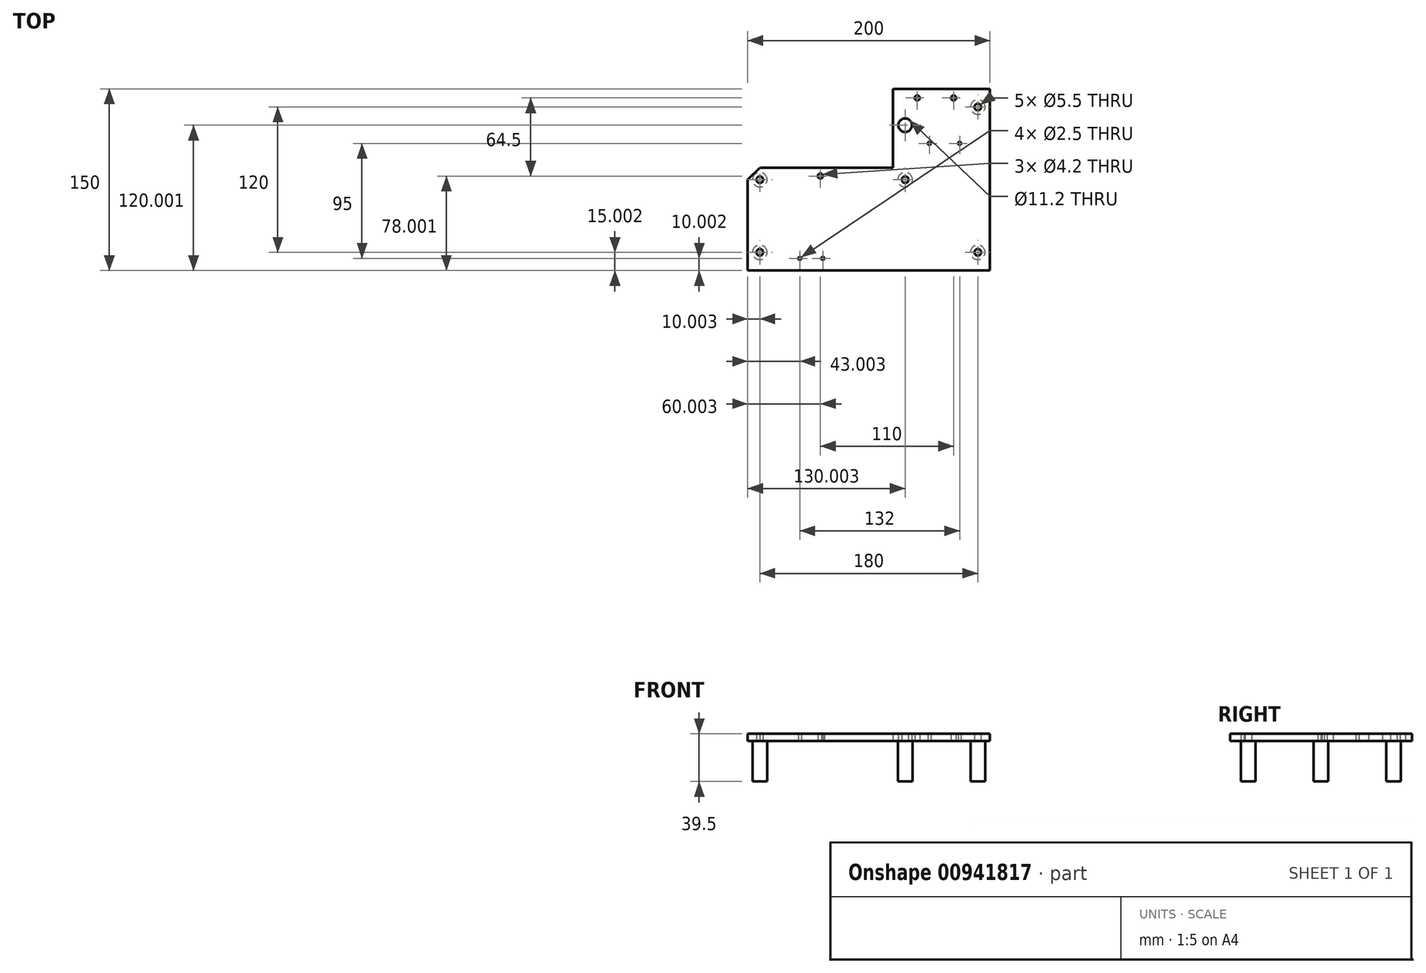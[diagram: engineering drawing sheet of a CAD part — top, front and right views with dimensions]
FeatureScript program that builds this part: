
annotation { "Feature Type Name" : "Feature", "Feature Type Description" : "" }
export const myFeature = defineFeature(function(context is Context, id is Id, definition is map)
    precondition{}
    {
        {
            var Q0;
            Q0=qCreatedBy(makeId("Top.planeOp"),FACE);
            var sketch = newSketch(context, id + "F0", { "sketchPlane" : qUnion([Q0])});
            skLineSegment(sketch, "E0", {"start": v(-126.29, 45.71) * mm, "end": v(-126.29, 110.71) * mm});
            skLineSegment(sketch, "E1", {"start": v(-46.29, 110.71) * mm, "end": v(-126.29, 110.71) * mm});
            skLineSegment(sketch, "E2", {"start": v(-46.29, -39.29) * mm, "end": v(-46.29, 110.71) * mm});
            skLineSegment(sketch, "E3", {"start": v(-246.29, -39.29) * mm, "end": v(-46.29, -39.29) * mm});
            skLineSegment(sketch, "E4", {"start": v(-246.29, 35.71) * mm, "end": v(-246.29, -39.29) * mm});
            skLineSegment(sketch, "E5", {"start": v(-236.29, 45.71) * mm, "end": v(-246.29, 35.71) * mm});
            skLineSegment(sketch, "E6", {"start": v(-236.29, 45.71) * mm, "end": v(-126.29, 45.71) * mm});
            skCircle(sketch, "E7", {"center": v(-116.29, 80.71) * mm, "radius": 5.6 * mm});
            skCircle(sketch, "E8", {"center": v(-106.29, 103.21) * mm, "radius": 2.1 * mm});
            skCircle(sketch, "E9", {"center": v(-76.29, 103.21) * mm, "radius": 2.1 * mm});
            skCircle(sketch, "E10", {"center": v(-71.29, 65.71) * mm, "radius": 1.25 * mm});
            skCircle(sketch, "E11", {"center": v(-96.29, 65.71) * mm, "radius": 1.25 * mm});
            skCircle(sketch, "E12", {"center": v(-184.29, -29.29) * mm, "radius": 1.25 * mm});
            skCircle(sketch, "E13", {"center": v(-203.29, -29.29) * mm, "radius": 1.25 * mm});
            skCircle(sketch, "E14", {"center": v(-186.29, 38.71) * mm, "radius": 2.1 * mm});
            skCircle(sketch, "E15", {"center": v(-236.29, 35.71) * mm, "radius": 2.75 * mm});
            skCircle(sketch, "E16", {"center": v(-56.29, -24.29) * mm, "radius": 2.75 * mm});
            skCircle(sketch, "E17", {"center": v(-116.29, 35.71) * mm, "radius": 2.75 * mm});
            skCircle(sketch, "E18", {"center": v(-56.29, 95.71) * mm, "radius": 2.75 * mm});
            skCircle(sketch, "E19", {"center": v(-116.29, 80.71) * mm, "radius": 2.75 * mm});
            skCircle(sketch, "E20", {"center": v(-236.29, -24.29) * mm, "radius": 2.75 * mm});
            skLineSegment(sketch, "E21", {"start": v(-116.29, 35.71) * mm, "end": v(-116.29, 38.21) * mm});
            skLineSegment(sketch, "E22", {"start": v(-116.29, 35.71) * mm, "end": v(-118.79, 35.71) * mm});
            skLineSegment(sketch, "E23", {"start": v(-116.29, 35.71) * mm, "end": v(-116.29, 33.21) * mm});
            skLineSegment(sketch, "E24", {"start": v(-116.29, 35.71) * mm, "end": v(-113.79, 35.71) * mm});
            skLineSegment(sketch, "E25", {"start": v(-116.29, 40.71) * mm, "end": v(-116.29, 40.96) * mm});
            skLineSegment(sketch, "E26", {"start": v(-121.29, 35.71) * mm, "end": v(-121.54, 35.71) * mm});
            skLineSegment(sketch, "E27", {"start": v(-116.29, 30.71) * mm, "end": v(-116.29, 30.46) * mm});
            skLineSegment(sketch, "E28", {"start": v(-111.29, 35.71) * mm, "end": v(-111.04, 35.71) * mm});
            skLineSegment(sketch, "E29", {"start": v(-116.29, 80.71) * mm, "end": v(-116.29, 83.21) * mm});
            skLineSegment(sketch, "E30", {"start": v(-116.29, 80.71) * mm, "end": v(-118.79, 80.71) * mm});
            skLineSegment(sketch, "E31", {"start": v(-116.29, 80.71) * mm, "end": v(-116.29, 78.21) * mm});
            skLineSegment(sketch, "E32", {"start": v(-116.29, 80.71) * mm, "end": v(-113.79, 80.71) * mm});
            skLineSegment(sketch, "E33", {"start": v(-116.29, 85.71) * mm, "end": v(-116.29, 85.96) * mm});
            skLineSegment(sketch, "E34", {"start": v(-121.29, 80.71) * mm, "end": v(-121.54, 80.71) * mm});
            skLineSegment(sketch, "E35", {"start": v(-116.29, 75.71) * mm, "end": v(-116.29, 75.46) * mm});
            skLineSegment(sketch, "E36", {"start": v(-111.29, 80.71) * mm, "end": v(-111.04, 80.71) * mm});
            skLineSegment(sketch, "E37", {"start": v(-56.29, 95.71) * mm, "end": v(-56.29, 98.21) * mm});
            skLineSegment(sketch, "E38", {"start": v(-56.29, 95.71) * mm, "end": v(-58.79, 95.71) * mm});
            skLineSegment(sketch, "E39", {"start": v(-56.29, 95.71) * mm, "end": v(-56.29, 93.21) * mm});
            skLineSegment(sketch, "E40", {"start": v(-56.29, 95.71) * mm, "end": v(-53.79, 95.71) * mm});
            skLineSegment(sketch, "E41", {"start": v(-56.29, 100.71) * mm, "end": v(-56.29, 100.96) * mm});
            skLineSegment(sketch, "E42", {"start": v(-61.29, 95.71) * mm, "end": v(-61.54, 95.71) * mm});
            skLineSegment(sketch, "E43", {"start": v(-56.29, 90.71) * mm, "end": v(-56.29, 90.46) * mm});
            skLineSegment(sketch, "E44", {"start": v(-51.29, 95.71) * mm, "end": v(-51.04, 95.71) * mm});
            skLineSegment(sketch, "E45", {"start": v(-56.29, -24.29) * mm, "end": v(-56.29, -21.79) * mm});
            skLineSegment(sketch, "E46", {"start": v(-56.29, -24.29) * mm, "end": v(-58.79, -24.29) * mm});
            skLineSegment(sketch, "E47", {"start": v(-56.29, -24.29) * mm, "end": v(-56.29, -26.79) * mm});
            skLineSegment(sketch, "E48", {"start": v(-56.29, -24.29) * mm, "end": v(-53.79, -24.29) * mm});
            skLineSegment(sketch, "E49", {"start": v(-56.29, -19.29) * mm, "end": v(-56.29, -19.04) * mm});
            skLineSegment(sketch, "E50", {"start": v(-61.29, -24.29) * mm, "end": v(-61.54, -24.29) * mm});
            skLineSegment(sketch, "E51", {"start": v(-56.29, -29.29) * mm, "end": v(-56.29, -29.54) * mm});
            skLineSegment(sketch, "E52", {"start": v(-51.29, -24.29) * mm, "end": v(-51.04, -24.29) * mm});
            skLineSegment(sketch, "E53", {"start": v(-236.29, 35.71) * mm, "end": v(-236.29, 38.21) * mm});
            skLineSegment(sketch, "E54", {"start": v(-236.29, 35.71) * mm, "end": v(-238.79, 35.71) * mm});
            skLineSegment(sketch, "E55", {"start": v(-236.29, 35.71) * mm, "end": v(-236.29, 33.21) * mm});
            skLineSegment(sketch, "E56", {"start": v(-236.29, 35.71) * mm, "end": v(-233.79, 35.71) * mm});
            skLineSegment(sketch, "E57", {"start": v(-236.29, 40.71) * mm, "end": v(-236.29, 40.96) * mm});
            skLineSegment(sketch, "E58", {"start": v(-241.29, 35.71) * mm, "end": v(-241.54, 35.71) * mm});
            skLineSegment(sketch, "E59", {"start": v(-236.29, 30.71) * mm, "end": v(-236.29, 30.46) * mm});
            skLineSegment(sketch, "E60", {"start": v(-231.29, 35.71) * mm, "end": v(-231.04, 35.71) * mm});
            skLineSegment(sketch, "E61", {"start": v(-236.29, -24.29) * mm, "end": v(-236.29, -21.79) * mm});
            skLineSegment(sketch, "E62", {"start": v(-236.29, -24.29) * mm, "end": v(-238.79, -24.29) * mm});
            skLineSegment(sketch, "E63", {"start": v(-236.29, -24.29) * mm, "end": v(-236.29, -26.79) * mm});
            skLineSegment(sketch, "E64", {"start": v(-236.29, -24.29) * mm, "end": v(-233.79, -24.29) * mm});
            skLineSegment(sketch, "E65", {"start": v(-236.29, -19.29) * mm, "end": v(-236.29, -19.04) * mm});
            skLineSegment(sketch, "E66", {"start": v(-241.29, -24.29) * mm, "end": v(-241.54, -24.29) * mm});
            skLineSegment(sketch, "E67", {"start": v(-236.29, -29.29) * mm, "end": v(-236.29, -29.54) * mm});
            skLineSegment(sketch, "E68", {"start": v(-231.29, -24.29) * mm, "end": v(-231.04, -24.29) * mm});
            skLineSegment(sketch, "E69", {"start": v(-106.29, 103.21) * mm, "end": v(-106.29, 105.71) * mm});
            skLineSegment(sketch, "E70", {"start": v(-106.29, 103.21) * mm, "end": v(-108.79, 103.21) * mm});
            skLineSegment(sketch, "E71", {"start": v(-106.29, 103.21) * mm, "end": v(-106.29, 100.71) * mm});
            skLineSegment(sketch, "E72", {"start": v(-106.29, 103.21) * mm, "end": v(-103.79, 103.21) * mm});
            skLineSegment(sketch, "E73", {"start": v(-106.29, 105.71) * mm, "end": v(-106.29, 107.81) * mm});
            skLineSegment(sketch, "E74", {"start": v(-108.79, 103.21) * mm, "end": v(-110.89, 103.21) * mm});
            skLineSegment(sketch, "E75", {"start": v(-106.29, 100.71) * mm, "end": v(-106.29, 98.61) * mm});
            skLineSegment(sketch, "E76", {"start": v(-103.79, 103.21) * mm, "end": v(-101.69, 103.21) * mm});
            skLineSegment(sketch, "E77", {"start": v(-76.29, 103.21) * mm, "end": v(-76.29, 105.71) * mm});
            skLineSegment(sketch, "E78", {"start": v(-76.29, 103.21) * mm, "end": v(-78.79, 103.21) * mm});
            skLineSegment(sketch, "E79", {"start": v(-76.29, 103.21) * mm, "end": v(-76.29, 100.71) * mm});
            skLineSegment(sketch, "E80", {"start": v(-76.29, 103.21) * mm, "end": v(-73.79, 103.21) * mm});
            skLineSegment(sketch, "E81", {"start": v(-76.29, 105.71) * mm, "end": v(-76.29, 107.81) * mm});
            skLineSegment(sketch, "E82", {"start": v(-78.79, 103.21) * mm, "end": v(-80.89, 103.21) * mm});
            skLineSegment(sketch, "E83", {"start": v(-76.29, 100.71) * mm, "end": v(-76.29, 98.61) * mm});
            skLineSegment(sketch, "E84", {"start": v(-73.79, 103.21) * mm, "end": v(-71.69, 103.21) * mm});
            skLineSegment(sketch, "E85", {"start": v(-71.29, 65.71) * mm, "end": v(-71.29, 68.21) * mm});
            skLineSegment(sketch, "E86", {"start": v(-71.29, 65.71) * mm, "end": v(-73.79, 65.71) * mm});
            skLineSegment(sketch, "E87", {"start": v(-71.29, 65.71) * mm, "end": v(-71.29, 63.21) * mm});
            skLineSegment(sketch, "E88", {"start": v(-71.29, 65.71) * mm, "end": v(-68.79, 65.71) * mm});
            skLineSegment(sketch, "E89", {"start": v(-71.29, 68.21) * mm, "end": v(-71.29, 69.46) * mm});
            skLineSegment(sketch, "E90", {"start": v(-73.79, 65.71) * mm, "end": v(-75.04, 65.71) * mm});
            skLineSegment(sketch, "E91", {"start": v(-71.29, 63.21) * mm, "end": v(-71.29, 61.96) * mm});
            skLineSegment(sketch, "E92", {"start": v(-68.79, 65.71) * mm, "end": v(-67.54, 65.71) * mm});
            skLineSegment(sketch, "E93", {"start": v(-96.29, 65.71) * mm, "end": v(-96.29, 68.21) * mm});
            skLineSegment(sketch, "E94", {"start": v(-96.29, 65.71) * mm, "end": v(-98.79, 65.71) * mm});
            skLineSegment(sketch, "E95", {"start": v(-96.29, 65.71) * mm, "end": v(-96.29, 63.21) * mm});
            skLineSegment(sketch, "E96", {"start": v(-96.29, 65.71) * mm, "end": v(-93.79, 65.71) * mm});
            skLineSegment(sketch, "E97", {"start": v(-96.29, 68.21) * mm, "end": v(-96.29, 69.46) * mm});
            skLineSegment(sketch, "E98", {"start": v(-98.79, 65.71) * mm, "end": v(-100.04, 65.71) * mm});
            skLineSegment(sketch, "E99", {"start": v(-96.29, 63.21) * mm, "end": v(-96.29, 61.96) * mm});
            skLineSegment(sketch, "E100", {"start": v(-93.79, 65.71) * mm, "end": v(-92.54, 65.71) * mm});
            skLineSegment(sketch, "E101", {"start": v(-184.29, -29.29) * mm, "end": v(-184.29, -26.79) * mm});
            skLineSegment(sketch, "E102", {"start": v(-184.29, -29.29) * mm, "end": v(-186.79, -29.29) * mm});
            skLineSegment(sketch, "E103", {"start": v(-184.29, -29.29) * mm, "end": v(-184.29, -31.79) * mm});
            skLineSegment(sketch, "E104", {"start": v(-184.29, -29.29) * mm, "end": v(-181.79, -29.29) * mm});
            skLineSegment(sketch, "E105", {"start": v(-184.29, -26.79) * mm, "end": v(-184.29, -25.54) * mm});
            skLineSegment(sketch, "E106", {"start": v(-186.79, -29.29) * mm, "end": v(-188.04, -29.29) * mm});
            skLineSegment(sketch, "E107", {"start": v(-184.29, -31.79) * mm, "end": v(-184.29, -33.04) * mm});
            skLineSegment(sketch, "E108", {"start": v(-181.79, -29.29) * mm, "end": v(-180.54, -29.29) * mm});
            skLineSegment(sketch, "E109", {"start": v(-203.29, -29.29) * mm, "end": v(-203.29, -26.79) * mm});
            skLineSegment(sketch, "E110", {"start": v(-203.29, -29.29) * mm, "end": v(-205.79, -29.29) * mm});
            skLineSegment(sketch, "E111", {"start": v(-203.29, -29.29) * mm, "end": v(-203.29, -31.79) * mm});
            skLineSegment(sketch, "E112", {"start": v(-203.29, -29.29) * mm, "end": v(-200.79, -29.29) * mm});
            skLineSegment(sketch, "E113", {"start": v(-203.29, -26.79) * mm, "end": v(-203.29, -25.54) * mm});
            skLineSegment(sketch, "E114", {"start": v(-205.79, -29.29) * mm, "end": v(-207.04, -29.29) * mm});
            skLineSegment(sketch, "E115", {"start": v(-203.29, -31.79) * mm, "end": v(-203.29, -33.04) * mm});
            skLineSegment(sketch, "E116", {"start": v(-200.79, -29.29) * mm, "end": v(-199.54, -29.29) * mm});
            skLineSegment(sketch, "E117", {"start": v(-186.29, 38.71) * mm, "end": v(-186.29, 41.21) * mm});
            skLineSegment(sketch, "E118", {"start": v(-186.29, 38.71) * mm, "end": v(-188.79, 38.71) * mm});
            skLineSegment(sketch, "E119", {"start": v(-186.29, 38.71) * mm, "end": v(-186.29, 36.21) * mm});
            skLineSegment(sketch, "E120", {"start": v(-186.29, 38.71) * mm, "end": v(-183.79, 38.71) * mm});
            skLineSegment(sketch, "E121", {"start": v(-186.29, 41.21) * mm, "end": v(-186.29, 43.31) * mm});
            skLineSegment(sketch, "E122", {"start": v(-188.79, 38.71) * mm, "end": v(-190.89, 38.71) * mm});
            skLineSegment(sketch, "E123", {"start": v(-186.29, 36.21) * mm, "end": v(-186.29, 34.11) * mm});
            skLineSegment(sketch, "E124", {"start": v(-183.79, 38.71) * mm, "end": v(-181.69, 38.71) * mm});
            skSolve(sketch);
        }
        {
            var Q0;
            Q0=makeQuery(id+"F0.imprint","IMPRINT",FACE,{"disambiguationData":[TD([[makeQuery(id+"F0.imprint","IMPRINT",EDGE,{"derivedFrom":sQuery(id+"F0.wireOp",EDGE,"E0")}),-1.0]])]});
            extrude(context, id + "F1", {"entities" : qUnion([Q0]), "depth" : 6 * mm, "offsetDistance" : 25 * mm});
        }
        {
            var Q0;
            Q0=makeQuery(id+"F1.opExtrude","CAP_FACE",FACE,{"disambiguationData":[OSD([sQuery(id+"F0.wireOp",EDGE,"E0"),sQuery(id+"F0.wireOp",EDGE,"E1"),sQuery(id+"F0.wireOp",EDGE,"E2"),sQuery(id+"F0.wireOp",EDGE,"E3"),sQuery(id+"F0.wireOp",EDGE,"E4"),sQuery(id+"F0.wireOp",EDGE,"E5"),sQuery(id+"F0.wireOp",EDGE,"E6"),sQuery(id+"F0.wireOp",EDGE,"E7"),sQuery(id+"F0.wireOp",EDGE,"E8"),sQuery(id+"F0.wireOp",EDGE,"E9"),sQuery(id+"F0.wireOp",EDGE,"E10"),sQuery(id+"F0.wireOp",EDGE,"E11"),sQuery(id+"F0.wireOp",EDGE,"E12"),sQuery(id+"F0.wireOp",EDGE,"E13"),sQuery(id+"F0.wireOp",EDGE,"E14"),sQuery(id+"F0.wireOp",EDGE,"E15"),sQuery(id+"F0.wireOp",EDGE,"E16"),sQuery(id+"F0.wireOp",EDGE,"E17"),sQuery(id+"F0.wireOp",EDGE,"E18"),sQuery(id+"F0.wireOp",EDGE,"E20")])],"isStart":true});
            var sketch = newSketch(context, id + "F2", { "sketchPlane" : qUnion([Q0])});
            skCircle(sketch, "E125", {"center": v(-236.29, 24.29) * mm, "radius": 6 * mm});
            skCircle(sketch, "E126", {"center": v(-236.29, -35.71) * mm, "radius": 6 * mm});
            skCircle(sketch, "E127", {"center": v(-56.29, 24.29) * mm, "radius": 6 * mm});
            skCircle(sketch, "E128", {"center": v(-56.29, -95.71) * mm, "radius": 6 * mm});
            skCircle(sketch, "E129", {"center": v(-116.29, -35.71) * mm, "radius": 6 * mm});
            skSolve(sketch);
        }
        {
            var Q0;
            Q0 = qSketchRegion(id + "F2", true);
            extrude(context, id + "F3", {"entities" : qUnion([Q0]), "depth" : 33.5 * mm, "offsetDistance" : 25 * mm});
        }
    });
